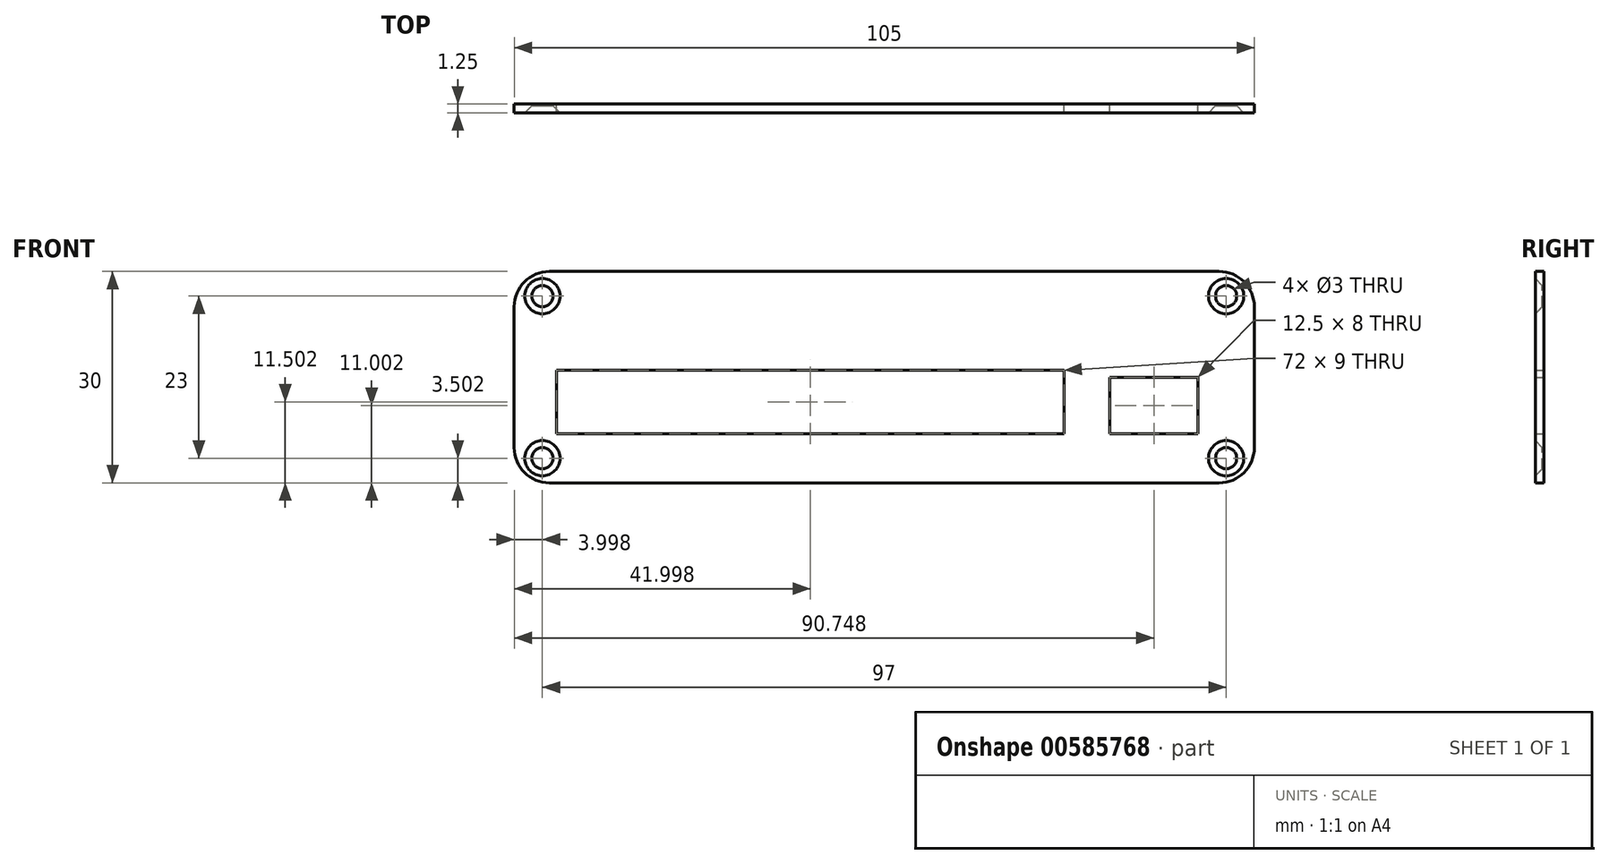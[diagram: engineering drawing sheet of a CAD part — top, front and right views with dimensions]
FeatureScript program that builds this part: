
annotation { "Feature Type Name" : "Feature", "Feature Type Description" : "" }
export const myFeature = defineFeature(function(context is Context, id is Id, definition is map)
    precondition{}
    {
        {
            var Q0;
            Q0=qCreatedBy(makeId("Front.planeOp"),FACE);
            var sketch = newSketch(context, id + "F0", { "sketchPlane" : qUnion([Q0])});
            skLineSegment(sketch, "E0.bottom", {"start": v(-35.94, 10.3) * mm, "end": v(69.06, 10.3) * mm});
            skLineSegment(sketch, "E0.top", {"start": v(-35.94, -19.7) * mm, "end": v(69.06, -19.7) * mm});
            skLineSegment(sketch, "E0.left", {"start": v(-35.94, 10.3) * mm, "end": v(-35.94, -19.7) * mm});
            skLineSegment(sketch, "E0.right", {"start": v(69.06, 10.3) * mm, "end": v(69.06, -19.7) * mm});
            skLineSegment(sketch, "E1.bottom", {"start": v(-29.94, -3.7) * mm, "end": v(42.06, -3.7) * mm});
            skLineSegment(sketch, "E1.top", {"start": v(-29.94, -12.7) * mm, "end": v(42.06, -12.7) * mm});
            skLineSegment(sketch, "E1.left", {"start": v(-29.94, -3.7) * mm, "end": v(-29.94, -12.7) * mm});
            skLineSegment(sketch, "E1.right", {"start": v(42.06, -3.7) * mm, "end": v(42.06, -12.7) * mm});
            skLineSegment(sketch, "E2.bottom", {"start": v(48.56, -4.7) * mm, "end": v(61.06, -4.7) * mm});
            skLineSegment(sketch, "E2.top", {"start": v(48.56, -12.7) * mm, "end": v(61.06, -12.7) * mm});
            skLineSegment(sketch, "E2.left", {"start": v(48.56, -4.7) * mm, "end": v(48.56, -12.7) * mm});
            skLineSegment(sketch, "E2.right", {"start": v(61.06, -4.7) * mm, "end": v(61.06, -12.7) * mm});
            skCircle(sketch, "E3", {"center": v(65.06, 6.8) * mm, "radius": 1.5 * mm});
            skCircle(sketch, "E4", {"center": v(65.06, -16.2) * mm, "radius": 1.5 * mm});
            skCircle(sketch, "E5", {"center": v(-31.94, 6.8) * mm, "radius": 1.5 * mm});
            skCircle(sketch, "E6", {"center": v(-31.94, -16.2) * mm, "radius": 1.5 * mm});
            skSolve(sketch);
        }
        {
            var Q0;
            Q0=makeQuery(id+"F0.imprint","IMPRINT",FACE,{"disambiguationData":[TD([[makeQuery(id+"F0.imprint","IMPRINT",EDGE,{"derivedFrom":sQuery(id+"F0.wireOp",EDGE,"E0.bottom")}),-1.0]])]});
            extrude(context, id + "F1", {"entities" : qUnion([Q0]), "depth" : 1.25 * mm, "offsetDistance" : 25 * mm});
        }
        {
            var Q0;
            Q0=makeQuery(id+"F1.opExtrude","SWEPT_EDGE",EDGE,{"disambiguationData":[OSD([sQuery(id+"F0.wireOp",EDGE,"E0.bottom"),sQuery(id+"F0.wireOp",EDGE,"E0.right")])]});
            var Q1;
            Q1=makeQuery(id+"F1.opExtrude","SWEPT_EDGE",EDGE,{"disambiguationData":[OSD([sQuery(id+"F0.wireOp",EDGE,"E0.top"),sQuery(id+"F0.wireOp",EDGE,"E0.right")])]});
            var Q2;
            Q2=makeQuery(id+"F1.opExtrude","SWEPT_EDGE",EDGE,{"disambiguationData":[OSD([sQuery(id+"F0.wireOp",EDGE,"E0.top"),sQuery(id+"F0.wireOp",EDGE,"E0.left")])]});
            var Q3;
            Q3=makeQuery(id+"F1.opExtrude","SWEPT_EDGE",EDGE,{"disambiguationData":[OSD([sQuery(id+"F0.wireOp",EDGE,"E0.bottom"),sQuery(id+"F0.wireOp",EDGE,"E0.left")])]});
            fillet(context, id + "F2", {"entities" : qUnion([Q0, Q1, Q2, Q3]), "radius" : 5 * mm, "tangentPropagation" : true, "allowEdgeOverflow" : false});
        }
        {
            var Q0;
            Q0=makeQuery(id+"F1.opExtrude","CAP_EDGE",EDGE,{"disambiguationData":[OSD([sQuery(id+"F0.wireOp",EDGE,"E5")])],"isStart":false});
            var Q1;
            Q1=makeQuery(id+"F1.opExtrude","CAP_EDGE",EDGE,{"disambiguationData":[OSD([sQuery(id+"F0.wireOp",EDGE,"E6")])],"isStart":false});
            var Q2;
            Q2=makeQuery(id+"F1.opExtrude","CAP_EDGE",EDGE,{"disambiguationData":[OSD([sQuery(id+"F0.wireOp",EDGE,"E4")])],"isStart":false});
            var Q3;
            Q3=makeQuery(id+"F1.opExtrude","CAP_EDGE",EDGE,{"disambiguationData":[OSD([sQuery(id+"F0.wireOp",EDGE,"E3")])],"isStart":false});
            chamfer(context, id + "F3", {"entities" : qUnion([Q0, Q1, Q2, Q3]), "width" : 1 * mm, "tangentPropagation" : true});
        }
    });
